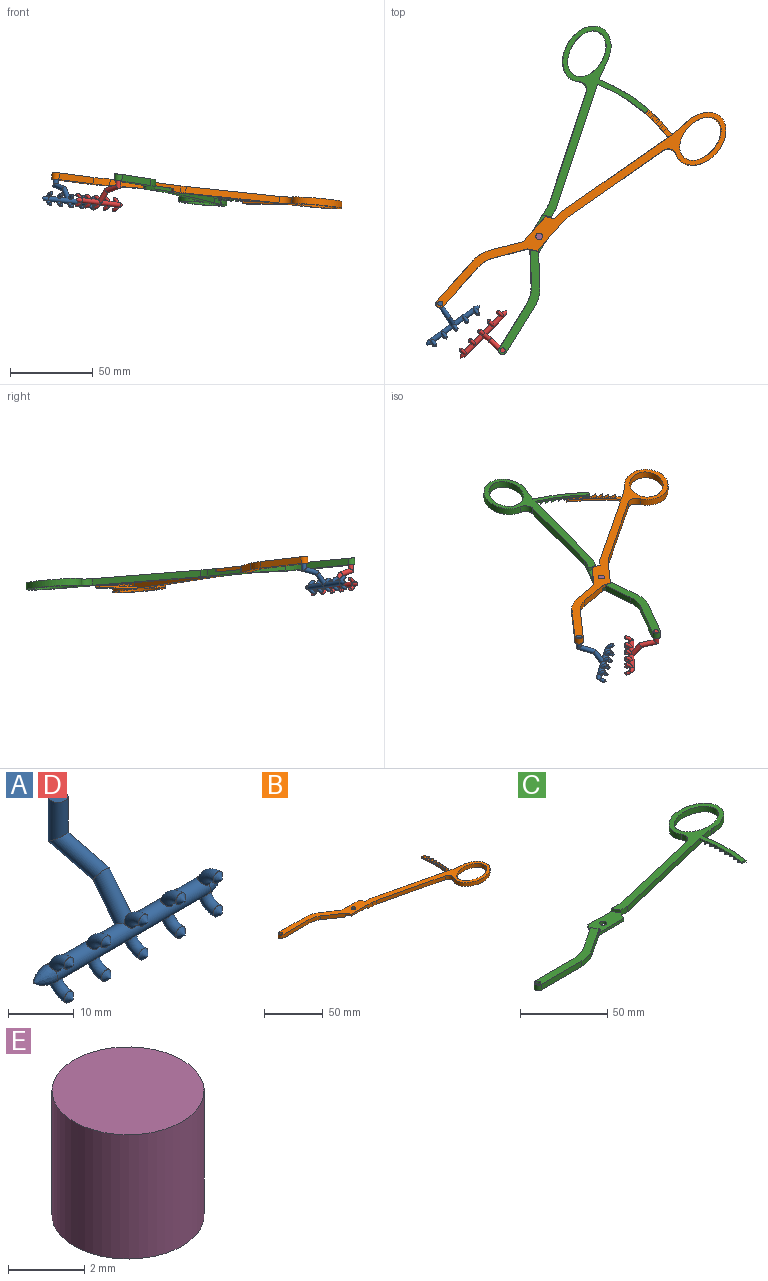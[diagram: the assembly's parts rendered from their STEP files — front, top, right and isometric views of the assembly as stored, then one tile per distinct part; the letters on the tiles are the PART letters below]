
ASSEMBLY  parts=5 mates=4
PART A: 32 faces, bbox 40x20.7x21.5 mm
  f0: torus R=3.14mm, axis (-1,0,0), area 23.1mm2, adj f1,f8,f13
  f1: cone r=1mm half-angle=45deg, axis (0,1,0), area 4.4mm2, adj f0
  f2: cylinder r=1.5mm len=8.62mm, axis (0,0,-1), area 70.2mm2, adj f3,f5
  f3: plane 3x3mm, normal (0,0,1), area 7.1mm2, adj f2
  f4: cylinder r=1.5mm len=9.39mm, axis (0,-0.61,-0.79), area 75.4mm2, adj f5,f8,f19
  f5: cylinder r=1.5mm len=11.66mm, axis (0,-0.97,-0.24), area 90.2mm2, adj f2,f4
  f6: plane 0.06x0.06mm, normal (1,0,0), area 0mm2, adj f10
  f7: plane 0.06x0.06mm, normal (-1,0,0), area 0mm2, adj f11
  f8: cylinder r=1.53mm len=32.86mm, axis (-1,0,0), area 278.9mm2, adj f0,f4,f9,f12,f13,f15,f16,f19
  f9: cylinder r=1.53mm len=0.52mm, axis (-1,0,0), area 0.1mm2, adj f8,f13,f31
  f10: cone r=1.53mm half-angle=45deg, axis (-1,0,0), area 0mm2, adj f6,f12
  f11: cone r=0.03mm half-angle=45deg, axis (1,0,0), area 0mm2, adj f7,f13
  f12: revolved ~3.54x3mm, area 48.2mm2, adj f8,f10,f27,f28
  f13: revolved ~3.54x3.06mm, area 24.8mm2, adj f0,f8,f9,f11,f31
  f14: cone r=1mm half-angle=45deg, axis (0,1,0), area 4.4mm2, adj f15
  f15: torus R=3.14mm, axis (-1,0,0), area 23.1mm2, adj f8,f14
  f16: torus R=3.14mm, axis (-1,0,0), area 22.2mm2, adj f8,f17
  f17: cone r=1mm half-angle=45deg, axis (0,1,0), area 4.4mm2, adj f16
  f18: cone r=1mm half-angle=45deg, axis (0,1,0), area 4.4mm2, adj f19
  f19: torus R=3.14mm, axis (-1,0,0), area 21mm2, adj f4,f8,f18
  f20: torus R=3.14mm, axis (-1,0,0), area 22.2mm2, adj f8,f21
  f21: cone r=1mm half-angle=45deg, axis (0,1,0), area 4.4mm2, adj f20
  f22: cone r=1mm half-angle=45deg, axis (0,1,0), area 4.4mm2, adj f23
  f23: torus R=3.14mm, axis (-1,0,0), area 23.1mm2, adj f8,f22
  f24: torus R=3.14mm, axis (-1,0,0), area 22.2mm2, adj f8,f25
  f25: cone r=1mm half-angle=45deg, axis (0,1,0), area 4.4mm2, adj f24
  f26: cone r=1mm half-angle=45deg, axis (0,1,0), area 4.4mm2, adj f27
  f27: torus R=3.14mm, axis (-1,0,0), area 22.4mm2, adj f8,f12,f26
  f28: torus R=3.14mm, axis (-1,0,0), area 23.2mm2, adj f8,f12,f29
  f29: cone r=1mm half-angle=45deg, axis (0,1,0), area 4.4mm2, adj f28
  f30: cone r=1mm half-angle=45deg, axis (0,1,0), area 4.4mm2, adj f31
  f31: torus R=3.14mm, axis (-1,0,0), area 22.3mm2, adj f8,f9,f13,f30
PART B: 88 faces, bbox 199.7x66.3x4 mm
  f0: plane 5x2.66mm, normal (0.88,0.47,0), area 11.3mm2, adj f1,f15,f19,f22
  f1: plane 19.64x4mm, normal (0,1,0), area 40.4mm2, adj f0,f3,f19,f21,f22,f87
  f2: plane 24.8x4mm, normal (0,-1,0), area 61mm2, adj f4,f10,f19,f20,f22,f82
  f3: plane 65.16x20mm, normal (0,0,-1), area 332mm2, adj f1,f5,f6,f7,f8,f9,f18,f21
  f4: plane 115.44x62.24mm, normal (0,0,-1), area 825.1mm2, adj f2,f11,f12,f13,f14,f15,f16,f20
  f5: plane 17.1x11.34mm, normal (0.55,0.83,0), area 82.1mm2, adj f3,f19,f85,f87
  f6: plane 32.85x4mm, normal (0,1,0), area 131.4mm2, adj f3,f7,f19,f85
  f7: cylinder r=2.5mm len=5mm, axis (0,0,1), area 31.4mm2, adj f3,f6,f8,f19
  f8: plane 31.35x4mm, normal (0,-1,0), area 125.4mm2, adj f3,f7,f19,f84
  f9: plane 17.6x11.67mm, normal (-0.55,-0.83,0), area 84.5mm2, adj f3,f10,f19,f21,f84
  f10: plane 5x2.66mm, normal (-0.88,-0.47,0), area 11.3mm2, adj f2,f9,f19,f22
  f11: plane 67.07x15.89mm, normal (-0.23,-0.97,0), area 275.7mm2, adj f4,f19,f82,f86
  f12: extruded ~35.95x25.96mm, area 309.9mm2, adj f4,f19,f83,f86
  f13: plane 8.16x4mm, normal (0.14,0.99,0), area 33mm2, adj f4,f14,f19,f83
  f14: plane 80x18.96mm, normal (0.23,0.97,0), area 325.1mm2, adj f4,f13,f15,f19,f23,f24,f25
  f15: plane 5.39x4mm, normal (0,1,0), area 21.6mm2, adj f0,f4,f14,f19,f20
  f16: extruded ~30x20mm, area 317.3mm2, adj f4,f19
  f17: cylinder r=2mm len=4mm, axis (0,0,1), area 25.1mm2, adj f19,f22
  f18: cylinder r=1.5mm len=4mm, axis (0,0,1), area 37.7mm2, adj f3,f19
  f19: plane 199.69x66.33mm, normal (0,0,1), area 1258.7mm2, adj f0,f1,f2,f5,f6,f7,f8,f9
  f20: plane 5x2.66mm, normal (-0.88,0.47,0), area 11.3mm2, adj f2,f4,f15,f22
  f21: plane 5x2.66mm, normal (0.88,-0.47,0), area 11.3mm2, adj f1,f3,f9,f22
  f22: plane 24.41x10mm, normal (0,0,-1), area 204.9mm2, adj f0,f1,f2,f10,f17,f20,f21
  f23: plane 7.78x3.72mm, normal (0,0,1), area 14.1mm2, adj f14,f24,f25,f79,f81
  f24: cylinder r=101.43mm len=34.86mm, axis (0,0,1), area 43.8mm2, adj f4,f14,f23,f26,f27,f28,f29,f30
  f25: cylinder r=98.43mm len=33.7mm, axis (0,0,1), area 42.3mm2, adj f4,f14,f23,f26,f27,f28,f29,f30
  f26: plane 4.13x3.11mm, normal (0,0,1), area 3.6mm2, adj f24,f25,f73,f75,f80
  f27: plane 4.02x3.08mm, normal (0,0,1), area 3.6mm2, adj f24,f25,f67,f69,f74
  f28: plane 3.91x3.04mm, normal (0,0,1), area 3.6mm2, adj f24,f25,f61,f63,f68
  f29: plane 3.8x3.08mm, normal (0,0,1), area 3.6mm2, adj f24,f25,f55,f57,f62
  f30: plane 3.8x3.23mm, normal (0,0,1), area 3.6mm2, adj f24,f25,f49,f51,f56
  f31: plane 3.79x3.37mm, normal (0,0,1), area 3.6mm2, adj f24,f25,f43,f45,f50
  f32: plane 3.77x3.5mm, normal (0,0,1), area 3.6mm2, adj f24,f25,f37,f39,f44
  f33: plane 2.96x1.25mm, normal (-0.16,0.99,0), area 3.7mm2, adj f4,f24,f25,f38
  f34: plane 2.65x0.42mm, normal (0,0,-1), area 0mm2, adj f24,f36,f39
  f35: plane 0.01x0mm, normal (0,0,-1), area 0mm2, adj f25,f37,f38
  f36: cylinder r=101.43mm len=2.65mm, axis (0,0,-1), area 1.9mm2, adj f34,f38,f39
  f37: cylinder r=98.43mm len=2.65mm, axis (0,0,-1), area 1.9mm2, adj f32,f35,f38,f39
  f38: plane 3.38x3.12mm, normal (-0.07,0.47,0.88), area 9.1mm2, adj f33,f35,f36,f37,f39
  f39: plane 2.96x1.44mm, normal (0.16,-0.99,0), area 4.3mm2, adj f32,f34,f36,f37,f38
  f40: plane 2.67x0.32mm, normal (0,0,-1), area 0mm2, adj f24,f42,f44,f45
  f41: plane 0.01x0mm, normal (0,0,-1), area 0mm2, adj f25,f43,f44
  f42: cylinder r=101.43mm len=2.66mm, axis (0,0,-1), area 1.9mm2, adj f40,f44,f45
  f43: cylinder r=98.43mm len=2.66mm, axis (0,0,-1), area 1.9mm2, adj f31,f41,f44,f45
  f44: plane 3.29x3.02mm, normal (-0.06,0.47,0.88), area 9.1mm2, adj f32,f40,f41,f42,f43,f45
  f45: plane 2.98x1.44mm, normal (0.12,-0.99,0), area 4.3mm2, adj f31,f40,f42,f43,f44
  f46: plane 2.67x0.21mm, normal (0,0,-1), area 0mm2, adj f24,f48,f50,f51
  f47: plane 0.01x0mm, normal (0,0,-1), area 0mm2, adj f25,f49,f50
  f48: cylinder r=101.43mm len=2.67mm, axis (0,0,-1), area 1.9mm2, adj f46,f50,f51
  f49: cylinder r=98.43mm len=2.67mm, axis (0,0,-1), area 1.9mm2, adj f30,f47,f50,f51
  f50: plane 3.2x2.91mm, normal (-0.04,0.47,0.88), area 9.1mm2, adj f31,f46,f47,f48,f49,f51
  f51: plane 2.99x1.44mm, normal (0.08,-1,0), area 4.3mm2, adj f30,f46,f48,f49,f50
  f52: plane 2.68x0.11mm, normal (0,0,-1), area 0mm2, adj f24,f54,f56,f57
  f53: plane 0.01x0mm, normal (0,0,-1), area 0mm2, adj f25,f55,f56
  f54: cylinder r=101.43mm len=2.68mm, axis (0,0,-1), area 1.9mm2, adj f52,f56,f57
  f55: cylinder r=98.43mm len=2.68mm, axis (0,0,-1), area 1.9mm2, adj f29,f53,f56,f57
  f56: plane 3.11x2.8mm, normal (-0.02,0.47,0.88), area 9.1mm2, adj f30,f52,f53,f54,f55,f57
  f57: plane 3x1.44mm, normal (0.04,-1,0), area 4.3mm2, adj f29,f52,f54,f55,f56
  f58: plane 2.68x0.04mm, normal (0,0,-1), area 0mm2, adj f24,f60,f62,f63
  f59: plane 0.01x0mm, normal (0,0,-1), area 0mm2, adj f25,f61,f62
  f60: cylinder r=101.43mm len=2.68mm, axis (0,0,-1), area 1.9mm2, adj f58,f62,f63
  f61: cylinder r=98.43mm len=2.68mm, axis (0,0,-1), area 1.9mm2, adj f28,f59,f62,f63
  f62: plane 3.01x2.69mm, normal (0,0.47,0.88), area 9.1mm2, adj f29,f58,f59,f60,f61,f63
  f63: plane 3x1.44mm, normal (0,-1,0), area 4.3mm2, adj f28,f58,f60,f61,f62
  f64: plane 2.68x0.13mm, normal (0,0,-1), area 0mm2, adj f24,f66,f68,f69
  f65: plane 0.01x0mm, normal (0,0,-1), area 0mm2, adj f25,f67,f68
  f66: cylinder r=101.43mm len=2.68mm, axis (0,0,-1), area 1.9mm2, adj f64,f68,f69
  f67: cylinder r=98.43mm len=2.68mm, axis (0,0,-1), area 1.9mm2, adj f27,f65,f68,f69
  f68: plane 3.1x2.79mm, normal (0.02,0.47,0.88), area 9.1mm2, adj f28,f64,f65,f66,f67,f69
  f69: plane 3x1.44mm, normal (-0.04,-1,0), area 4.3mm2, adj f27,f64,f66,f67,f68
  f70: plane 2.67x0.24mm, normal (0,0,-1), area 0mm2, adj f24,f72,f74,f75
  f71: plane 0.01x0mm, normal (0,0,-1), area 0mm2, adj f25,f73,f74
  f72: cylinder r=101.43mm len=2.67mm, axis (0,0,-1), area 1.9mm2, adj f70,f74,f75
  f73: cylinder r=98.43mm len=2.67mm, axis (0,0,-1), area 1.9mm2, adj f26,f71,f74,f75
  f74: plane 3.2x2.9mm, normal (0.04,0.47,0.88), area 9.1mm2, adj f27,f70,f71,f72,f73,f75
  f75: plane 2.99x1.44mm, normal (-0.07,-1,0), area 4.3mm2, adj f26,f70,f72,f73,f74
  f76: plane 2.66x0.34mm, normal (0,0,-1), area 0mm2, adj f24,f78,f80,f81
  f77: plane 0.01x0mm, normal (0,0,-1), area 0mm2, adj f25,f79,f80
  f78: cylinder r=101.43mm len=2.66mm, axis (0,0,-1), area 1.9mm2, adj f76,f80,f81
  f79: cylinder r=98.43mm len=2.66mm, axis (0,0,-1), area 1.9mm2, adj f23,f77,f80,f81
  f80: plane 3.29x3mm, normal (0.05,0.47,0.88), area 9.1mm2, adj f26,f76,f77,f78,f79,f81
  f81: plane 2.98x1.44mm, normal (-0.11,-0.99,0), area 4.3mm2, adj f23,f76,f78,f79,f80
  f82: cylinder r=20mm len=4.61mm, axis (0,0,1), area 18.6mm2, adj f2,f4,f11,f19
  f83: cylinder r=20mm len=4mm, axis (0,0,1), area 8.6mm2, adj f4,f12,f13,f19
  f84: cylinder r=20mm len=11.05mm, axis (0,0,-1), area 46.8mm2, adj f3,f8,f9,f19
  f85: cylinder r=20mm len=11.05mm, axis (0,0,1), area 46.8mm2, adj f3,f5,f6,f19
  f86: cylinder r=5mm len=7.22mm, axis (0,0,1), area 36.6mm2, adj f4,f11,f12,f19
  f87: cylinder r=2mm len=4mm, axis (0,0,-1), area 4.7mm2, adj f1,f3,f5,f19
PART C: 89 faces, bbox 199.7x66.3x4 mm
  f0: plane 17.1x11.34mm, normal (0.55,-0.83,0), area 82.1mm2, adj f8,f9,f86,f88
  f1: plane 19.64x4mm, normal (0,-1,0), area 40.4mm2, adj f2,f8,f9,f19,f22,f88
  f2: plane 5x2.66mm, normal (0.88,0.47,0), area 11.3mm2, adj f1,f3,f8,f22
  f3: plane 17.6x11.67mm, normal (-0.55,0.83,0), area 84.5mm2, adj f2,f8,f9,f20,f85
  f4: plane 31.35x4mm, normal (0,1,0), area 125.4mm2, adj f5,f8,f9,f85
  f5: cylinder r=2.5mm len=5mm, axis (0,0,-1), area 31.4mm2, adj f4,f6,f8,f9
  f6: plane 32.85x4mm, normal (0,-1,0), area 131.4mm2, adj f5,f8,f9,f86
  f7: cylinder r=1.5mm len=4mm, axis (0,0,-1), area 37.7mm2, adj f8,f9
  f8: plane 65.16x20mm, normal (0,0,1), area 332mm2, adj f0,f1,f2,f3,f4,f5,f6,f7
  f9: plane 199.69x66.33mm, normal (0,0,-1), area 1258.7mm2, adj f0,f1,f3,f4,f5,f6,f7,f10
  f10: extruded ~35.95x25.96mm, area 309.9mm2, adj f9,f18,f83,f87
  f11: plane 67.07x15.89mm, normal (-0.23,0.97,0), area 275.7mm2, adj f9,f18,f84,f87
  f12: plane 24.8x4mm, normal (0,1,0), area 61mm2, adj f9,f13,f18,f20,f22,f84
  f13: plane 5x2.66mm, normal (-0.88,-0.47,0), area 11.3mm2, adj f12,f14,f18,f22
  f14: plane 5.39x4mm, normal (0,-1,0), area 21.6mm2, adj f9,f13,f15,f18,f19
  f15: plane 80x18.96mm, normal (0.23,-0.97,0), area 325.1mm2, adj f9,f14,f17,f18,f23,f24,f25
  f16: extruded ~30x20mm, area 317.3mm2, adj f9,f18
  f17: plane 8.16x4mm, normal (0.14,-0.99,0), area 33mm2, adj f9,f15,f18,f83
  f18: plane 115.44x62.12mm, normal (0,0,1), area 824.8mm2, adj f10,f11,f12,f13,f14,f15,f16,f17
  f19: plane 5x2.66mm, normal (0.88,-0.47,0), area 11.3mm2, adj f1,f9,f14,f22
  f20: plane 5x2.66mm, normal (-0.88,0.47,0), area 11.3mm2, adj f3,f9,f12,f22
  f21: cylinder r=2mm len=4mm, axis (0,0,1), area 25.1mm2, adj f9,f22
  f22: plane 24.41x10mm, normal (0,0,1), area 204.9mm2, adj f1,f2,f12,f13,f19,f20,f21
  f23: plane 3.89x3.52mm, normal (0,0,-1), area 10.1mm2, adj f15,f24,f25,f40
  f24: cylinder r=98.43mm len=33.59mm, axis (0,0,-1), area 42.2mm2, adj f15,f18,f23,f26,f27,f28,f29,f30
  f25: cylinder r=101.43mm len=34.74mm, axis (0,0,-1), area 43.7mm2, adj f15,f18,f23,f26,f27,f28,f29,f30
  f26: plane 4.23x3.15mm, normal (0,0,-1), area 3.7mm2, adj f24,f25,f34,f79,f81
  f27: plane 4.14x3.12mm, normal (0,0,-1), area 3.7mm2, adj f24,f25,f73,f75,f82
  f28: plane 4.03x3.08mm, normal (0,0,-1), area 3.7mm2, adj f24,f25,f67,f69,f76
  f29: plane 3.92x3.04mm, normal (0,0,-1), area 3.7mm2, adj f24,f25,f61,f63,f70
  f30: plane 3.81x3.07mm, normal (0,0,-1), area 3.7mm2, adj f24,f25,f55,f57,f64
  f31: plane 3.8x3.21mm, normal (0,0,-1), area 3.7mm2, adj f24,f25,f49,f51,f58
  f32: plane 3.79x3.35mm, normal (0,0,-1), area 3.7mm2, adj f24,f25,f43,f45,f52
  f33: plane 3.77x3.49mm, normal (0,0,-1), area 3.7mm2, adj f24,f25,f37,f39,f46
  f34: plane 2.96x1.25mm, normal (-0.16,-0.99,0), area 3.7mm2, adj f18,f24,f25,f26
  f35: plane 2.63x0.41mm, normal (0,0,1), area 0mm2, adj f25,f36,f39
  f36: cylinder r=101.43mm len=2.63mm, axis (0,0,-1), area 1.9mm2, adj f35,f39,f40
  f37: cylinder r=98.43mm len=2.63mm, axis (0,0,-1), area 1.9mm2, adj f33,f38,f39,f40
  f38: plane 0.01x0mm, normal (0,0,1), area 0mm2, adj f24,f37,f40
  f39: plane 3.37x3.09mm, normal (0.07,-0.47,-0.88), area 9.1mm2, adj f33,f35,f36,f37,f40
  f40: plane 2.97x1.43mm, normal (-0.15,0.99,0), area 4.3mm2, adj f23,f36,f37,f38,f39
  f41: plane 0.01x0mm, normal (0,0,1), area 0mm2, adj f24,f43,f46
  f42: cylinder r=101.43mm len=2.64mm, axis (0,0,-1), area 1.9mm2, adj f44,f45,f46
  f43: cylinder r=98.43mm len=2.64mm, axis (0,0,-1), area 1.9mm2, adj f32,f41,f45,f46
  f44: plane 2.65x0.31mm, normal (0,0,1), area 0mm2, adj f25,f42,f45,f46
  f45: plane 3.29x2.99mm, normal (0.05,-0.47,-0.88), area 9.1mm2, adj f32,f42,f43,f44,f46
  f46: plane 2.98x1.43mm, normal (-0.11,0.99,0), area 4.3mm2, adj f33,f41,f42,f43,f44,f45
  f47: plane 0.01x0mm, normal (0,0,1), area 0mm2, adj f24,f49,f52
  f48: cylinder r=101.43mm len=2.65mm, axis (0,0,-1), area 1.9mm2, adj f50,f51,f52
  f49: cylinder r=98.43mm len=2.65mm, axis (0,0,-1), area 1.9mm2, adj f31,f47,f51,f52
  f50: plane 2.66x0.2mm, normal (0,0,1), area 0mm2, adj f25,f48,f51,f52
  f51: plane 3.2x2.88mm, normal (0.04,-0.47,-0.88), area 9.1mm2, adj f31,f48,f49,f50,f52
  f52: plane 2.99x1.43mm, normal (-0.08,1,0), area 4.3mm2, adj f32,f47,f48,f49,f50,f51
  f53: plane 0.01x0mm, normal (0,0,1), area 0mm2, adj f24,f55,f58
  f54: cylinder r=101.43mm len=2.66mm, axis (0,0,-1), area 1.9mm2, adj f56,f57,f58
  f55: cylinder r=98.43mm len=2.66mm, axis (0,0,-1), area 1.9mm2, adj f30,f53,f57,f58
  f56: plane 2.66x0.1mm, normal (0,0,1), area 0mm2, adj f25,f54,f57,f58
  f57: plane 3.1x2.77mm, normal (0.02,-0.47,-0.88), area 9.1mm2, adj f30,f54,f55,f56,f58
  f58: plane 3x1.43mm, normal (-0.04,1,0), area 4.3mm2, adj f31,f53,f54,f55,f56,f57
  f59: plane 0.01x0mm, normal (0,0,1), area 0mm2, adj f24,f61,f64
  f60: cylinder r=101.43mm len=2.66mm, axis (0,0,-1), area 1.9mm2, adj f62,f63,f64
  f61: cylinder r=98.43mm len=2.66mm, axis (0,0,-1), area 1.9mm2, adj f29,f59,f63,f64
  f62: plane 2.66x0.05mm, normal (0,0,1), area 0mm2, adj f25,f60,f63,f64
  f63: plane 3.01x2.66mm, normal (0,-0.47,-0.88), area 9.1mm2, adj f29,f60,f61,f62,f64
  f64: plane 3x1.43mm, normal (0,1,0), area 4.3mm2, adj f30,f59,f60,f61,f62,f63
  f65: plane 0.01x0mm, normal (0,0,1), area 0mm2, adj f24,f67,f70
  f66: cylinder r=101.43mm len=2.66mm, axis (0,0,-1), area 1.9mm2, adj f68,f69,f70
  f67: cylinder r=98.43mm len=2.66mm, axis (0,0,-1), area 1.9mm2, adj f28,f65,f69,f70
  f68: plane 2.66x0.14mm, normal (0,0,1), area 0mm2, adj f25,f66,f69,f70
  f69: plane 3.1x2.78mm, normal (-0.02,-0.47,-0.88), area 9.1mm2, adj f28,f66,f67,f68,f70
  f70: plane 3x1.43mm, normal (0.04,1,0), area 4.3mm2, adj f29,f65,f66,f67,f68,f69
  f71: plane 0.01x0mm, normal (0,0,1), area 0mm2, adj f24,f73,f76
  f72: cylinder r=101.43mm len=2.65mm, axis (0,0,-1), area 1.9mm2, adj f74,f75,f76
  f73: cylinder r=98.43mm len=2.65mm, axis (0,0,-1), area 1.9mm2, adj f27,f71,f75,f76
  f74: plane 2.65x0.24mm, normal (0,0,1), area 0mm2, adj f25,f72,f75,f76
  f75: plane 3.2x2.89mm, normal (-0.04,-0.47,-0.88), area 9.1mm2, adj f27,f72,f73,f74,f76
  f76: plane 2.99x1.43mm, normal (0.08,1,0), area 4.3mm2, adj f28,f71,f72,f73,f74,f75
  f77: plane 0.01x0mm, normal (0,0,1), area 0mm2, adj f24,f79,f82
  f78: cylinder r=101.43mm len=2.64mm, axis (0,0,-1), area 1.9mm2, adj f80,f81,f82
  f79: cylinder r=98.43mm len=2.64mm, axis (0,0,-1), area 1.9mm2, adj f26,f77,f81,f82
  f80: plane 2.64x0.35mm, normal (0,0,1), area 0mm2, adj f25,f78,f81,f82
  f81: plane 3.29x2.99mm, normal (-0.06,-0.47,-0.88), area 9.1mm2, adj f26,f78,f79,f80,f82
  f82: plane 2.98x1.43mm, normal (0.12,0.99,0), area 4.3mm2, adj f27,f77,f78,f79,f80,f81
  f83: cylinder r=20mm len=4mm, axis (0,0,-1), area 8.6mm2, adj f9,f10,f17,f18
  f84: cylinder r=20mm len=4.61mm, axis (0,0,-1), area 18.6mm2, adj f9,f11,f12,f18
  f85: cylinder r=20mm len=11.05mm, axis (0,0,1), area 46.8mm2, adj f3,f4,f8,f9
  f86: cylinder r=20mm len=11.05mm, axis (0,0,-1), area 46.8mm2, adj f0,f6,f8,f9
  f87: cylinder r=5mm len=7.22mm, axis (0,0,-1), area 36.6mm2, adj f9,f10,f11,f18
  f88: cylinder r=2mm len=4mm, axis (0,0,1), area 4.7mm2, adj f0,f1,f8,f9
PART D: same geometry as A
PART E: 3 faces, bbox 4x4x4 mm
  f0: cylinder r=2mm len=4mm, axis (0,0,-1), area 50.3mm2, adj f1,f2
  f1: plane 4x4mm, normal (0,0,1), area 12.6mm2, adj f0
  f2: plane 4x4mm, normal (0,0,-1), area 12.6mm2, adj f0
PLACE A rot(axis=(-0.05,0.13,0.99),36.5deg) t=(37.36,-215.02,52.06)mm
PLACE B rot(axis=(-0.03,0.1,0.99),48.5deg) t=(31.59,-203.18,51.76)mm
PLACE C rot(axis=(-0.02,0.09,1),58.4deg) t=(33,-204.24,51.73)mm
PLACE D rot(axis=(-0.04,-0.01,-1),134.6deg) t=(-37.96,-294.65,61.61)mm
PLACE E rot(axis=(-0.05,0.12,0.99),37.8deg) t=(30.3,-201.79,51.76)mm
MATE revolute C.f21 <-> B.f17  axis (0.07,0.06,1) through (38.3,-195.67,50.89)mm
MATE revolute E.f0 <-> B.f17  axis (-0.07,-0.06,-1) through (38.43,-195.56,52.88)mm
MATE revolute A.f2 <-> B.f7  axis (0.07,0.06,1) through (-21.12,-236.01,59.13)mm
MATE revolute D.f2 <-> C.f5  axis (0.07,0.06,1) through (16.57,-264.22,58.27)mm
